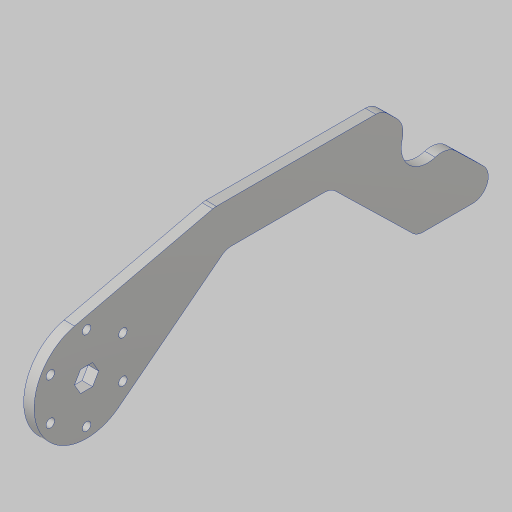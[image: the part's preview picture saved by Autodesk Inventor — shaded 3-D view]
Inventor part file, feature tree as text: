
AUTODESK INVENTOR PART (.ipt)
format: ipt  version: 2023.5 (Build 275446000, 446)  size: 163,840 bytes
history: native  units: in
note: dims shown in document units (in); Inventor stores cm internally (conversion verified against a paired STEP export)
features: sketch x4, extrude x2, fillet x2, hole x1
ambient origin geometry x8: Origin, YZ Plane, XZ Plane, XY Plane, X Axis, Y Axis, Z Axis, Center Point
bodies: Solid1 (feature_tree)
feature tree (9):
  sketch  "Sketch1"  dims[d0=2.5in d2=5.0in]
  extrude  "Extrusion1"  Depth=5.0in
  hole  "Hole1"  [1 undecoded]
  extrude  "Extrusion2"  Depth=0.25in
  fillet  "Fillet1"  Radius=1.0in
  fillet  "Fillet2"  Radius=0.25in
  sketch  "Sketch2"  dims[d3=2.3037in d4=0.75in]
  sketch  "Sketch3"  dims[d5=6.385in d6=8.0in d7=1.0in d8=0.25in]
  sketch  "Sketch4"  dims[d9=2.5in d10=1.0in d11=4.0in d12=0.5in d13=2.25in d14=0.25in d15=0.0in d16=2.0in d17=2.3622in d19=360.0deg d21=0.201in d22=0.38in d23=0.385in d24=0.25in d25=0.5635in d26=1.0in d27=0.8108in d28=1.5in d29=0.75in d30=1.25in d31=2.0in d32=0.25in d33=0.0in d34=0.0in d35=0.5in d36=0.375in]
note: 1 required parameter value undecoded (feature->parameter linkage not recoverable at this tier; creation-order binding heuristic only, values carry confidence <= 0.55)
